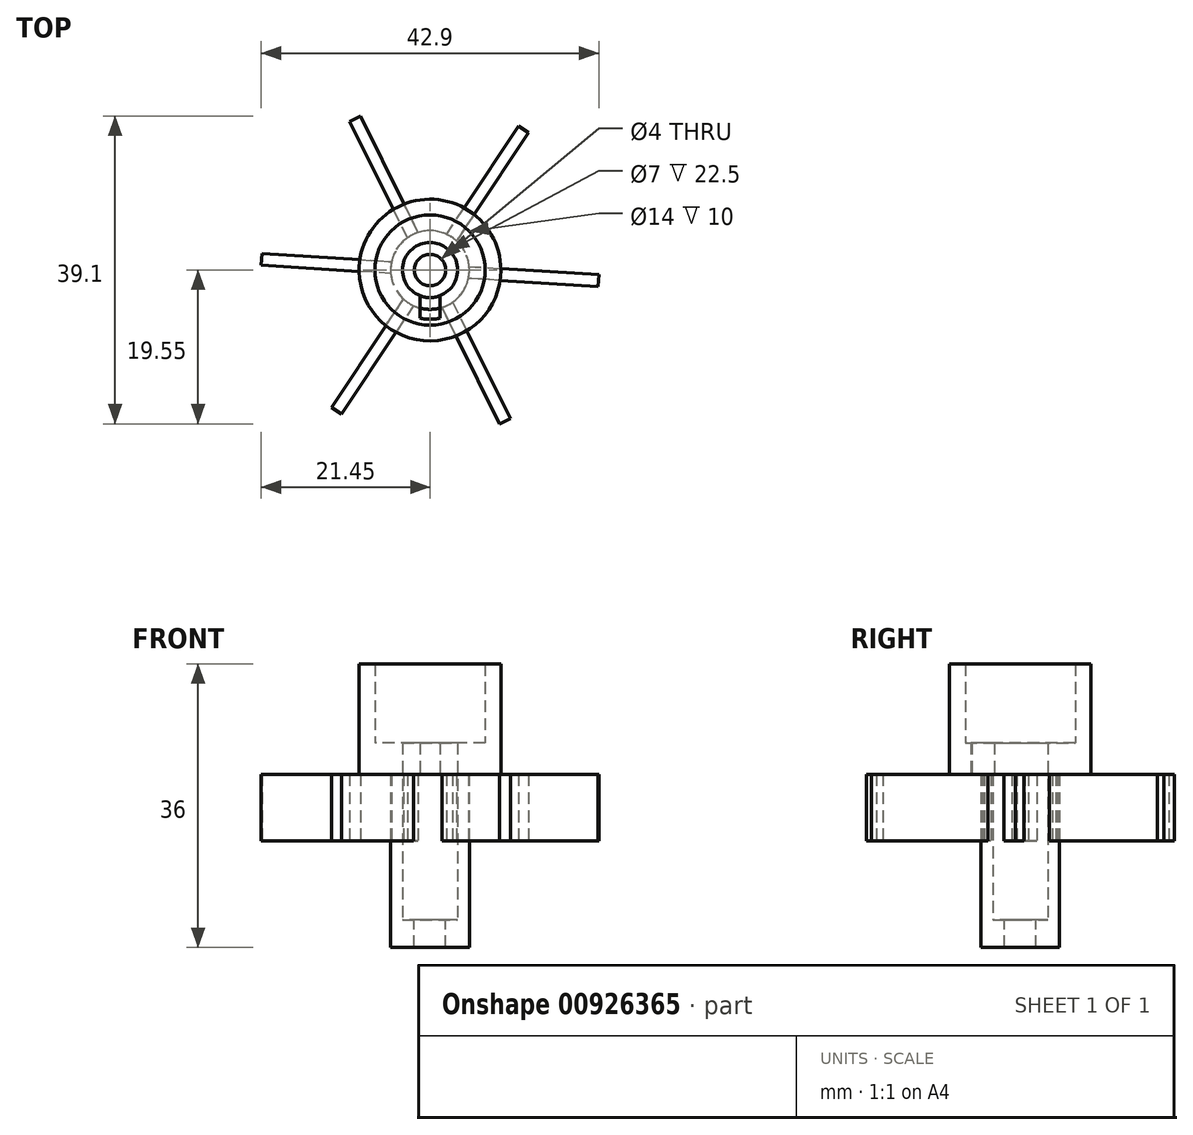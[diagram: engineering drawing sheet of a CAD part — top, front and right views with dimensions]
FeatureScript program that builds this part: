
annotation { "Feature Type Name" : "Feature", "Feature Type Description" : "" }
export const myFeature = defineFeature(function(context is Context, id is Id, definition is map)
    precondition{}
    {
        {
            var Q0;
            Q0=qCreatedBy(makeId("Top.planeOp"),FACE);
            var sketch = newSketch(context, id + "F0", { "sketchPlane" : qUnion([Q0])});
            skCircle(sketch, "E0", {"center": v(0, 0) * mm, "radius": 5 * mm});
            skCircle(sketch, "E1", {"center": v(0, 0) * mm, "radius": 3.5 * mm});
            skLineSegment(sketch, "E2", {"start": v(0, 0) * mm, "end": v(-28.81, 1.83) * mm, "construction": true});
            skLineSegment(sketch, "E3", {"start": v(-4.98, -0.44) * mm, "end": v(-21.45, 0.6) * mm});
            skLineSegment(sketch, "E4", {"start": v(-21.45, 0.6) * mm, "end": v(-21.35, 2.1) * mm});
            skLineSegment(sketch, "E5", {"start": v(-21.35, 2.1) * mm, "end": v(-4.89, 1.06) * mm});
            skLineSegment(sketch, "E6.1.0", {"start": v(-12.5, -17.44) * mm, "end": v(-3.36, -3.7) * mm});
            skLineSegment(sketch, "E6.1.1", {"start": v(-2.11, -4.53) * mm, "end": v(-11.25, -18.27) * mm});
            skLineSegment(sketch, "E6.1.2", {"start": v(-11.25, -18.27) * mm, "end": v(-12.5, -17.44) * mm});
            skLineSegment(sketch, "E6.2.0", {"start": v(8.85, -19.55) * mm, "end": v(1.52, -4.76) * mm});
            skLineSegment(sketch, "E6.2.1", {"start": v(2.87, -4.1) * mm, "end": v(10.2, -18.88) * mm});
            skLineSegment(sketch, "E6.2.2", {"start": v(10.2, -18.88) * mm, "end": v(8.85, -19.55) * mm});
            skLineSegment(sketch, "E6.3.0", {"start": v(21.35, -2.1) * mm, "end": v(4.89, -1.06) * mm});
            skLineSegment(sketch, "E6.3.1", {"start": v(4.98, 0.44) * mm, "end": v(21.45, -0.6) * mm});
            skLineSegment(sketch, "E6.3.2", {"start": v(21.45, -0.6) * mm, "end": v(21.35, -2.1) * mm});
            skLineSegment(sketch, "E6.4.0", {"start": v(12.5, 17.44) * mm, "end": v(3.36, 3.7) * mm});
            skLineSegment(sketch, "E6.4.1", {"start": v(2.11, 4.53) * mm, "end": v(11.25, 18.27) * mm});
            skLineSegment(sketch, "E6.4.2", {"start": v(11.25, 18.27) * mm, "end": v(12.5, 17.44) * mm});
            skLineSegment(sketch, "E6.5.0", {"start": v(-8.85, 19.55) * mm, "end": v(-1.52, 4.76) * mm});
            skLineSegment(sketch, "E6.5.1", {"start": v(-2.87, 4.1) * mm, "end": v(-10.2, 18.88) * mm});
            skLineSegment(sketch, "E6.5.2", {"start": v(-10.2, 18.88) * mm, "end": v(-8.85, 19.55) * mm});
            skCircle(sketch, "E7", {"center": v(0, 0) * mm, "radius": 2 * mm});
            skSolve(sketch);
        }
        {
            var Q0;
            {var subQ0=sQuery(id+"F0.wireOp",EDGE,"E3");Q0=makeQuery(id+"F0.imprint","IMPRINT",FACE,{"disambiguationData":[TD([[makeQuery(id+"F0.imprint","IMPRINT",EDGE,{"derivedFrom":subQ0}),-1.0]])]});}
            var Q1;
            Q1=makeQuery(id+"F0.imprint","IMPRINT",FACE,{"disambiguationData":[TD([[makeQuery(id+"F0.imprint","IMPRINT",EDGE,{"derivedFrom":sQuery(id+"F0.wireOp",EDGE,"E1")}),-1.0]])]});
            var Q2;
            {var subQ0=sQuery(id+"F0.wireOp",EDGE,"E6.5.0");Q2=makeQuery(id+"F0.imprint","IMPRINT",FACE,{"disambiguationData":[TD([[makeQuery(id+"F0.imprint","IMPRINT",EDGE,{"derivedFrom":subQ0}),-1.0]])]});}
            var Q3;
            {var subQ0=sQuery(id+"F0.wireOp",EDGE,"E6.4.0");Q3=makeQuery(id+"F0.imprint","IMPRINT",FACE,{"disambiguationData":[TD([[makeQuery(id+"F0.imprint","IMPRINT",EDGE,{"derivedFrom":subQ0}),-1.0]])]});}
            var Q4;
            {var subQ0=sQuery(id+"F0.wireOp",EDGE,"E6.3.0");Q4=makeQuery(id+"F0.imprint","IMPRINT",FACE,{"disambiguationData":[TD([[makeQuery(id+"F0.imprint","IMPRINT",EDGE,{"derivedFrom":subQ0}),-1.0]])]});}
            var Q5;
            {var subQ0=sQuery(id+"F0.wireOp",EDGE,"E6.2.0");Q5=makeQuery(id+"F0.imprint","IMPRINT",FACE,{"disambiguationData":[TD([[makeQuery(id+"F0.imprint","IMPRINT",EDGE,{"derivedFrom":subQ0}),-1.0]])]});}
            var Q6;
            {var subQ0=sQuery(id+"F0.wireOp",EDGE,"E6.1.0");Q6=makeQuery(id+"F0.imprint","IMPRINT",FACE,{"disambiguationData":[TD([[makeQuery(id+"F0.imprint","IMPRINT",EDGE,{"derivedFrom":subQ0}),-1.0]])]});}
            extrude(context, id + "F1", {"entities" : qUnion([Q0, Q1, Q2, Q3, Q4, Q5, Q6]), "depth" : 8.5 * mm, "offsetDistance" : 25 * mm});
        }
        {
            var Q0;
            Q0=makeQuery(id+"F0.imprint","IMPRINT",FACE,{"disambiguationData":[TD([[makeQuery(id+"F0.imprint","IMPRINT",EDGE,{"derivedFrom":sQuery(id+"F0.wireOp",EDGE,"E1")}),1.0]])]});
            var Q1;
            Q1=makeQuery(id+"F0.imprint","IMPRINT",FACE,{"disambiguationData":[TD([[makeQuery(id+"F0.imprint","IMPRINT",EDGE,{"derivedFrom":sQuery(id+"F0.wireOp",EDGE,"E1")}),-1.0]])]});
            extrude(context, id + "F2", {"entities" : qUnion([Q0, Q1]), "operationType" : NewBodyOperationType.ADD, "oppositeDirection" : true, "depth" : 13.5 * mm, "offsetDistance" : 25 * mm});
        }
        {
            var Q0;
            Q0=makeQuery(id+"F1.opExtrude","CAP_FACE",FACE,{"disambiguationData":[OSD([sQuery(id+"F0.wireOp",EDGE,"E0"),sQuery(id+"F0.wireOp",EDGE,"E1"),sQuery(id+"F0.wireOp",EDGE,"E3"),sQuery(id+"F0.wireOp",EDGE,"E4"),sQuery(id+"F0.wireOp",EDGE,"E5"),sQuery(id+"F0.wireOp",EDGE,"E6.1.0"),sQuery(id+"F0.wireOp",EDGE,"E6.1.1"),sQuery(id+"F0.wireOp",EDGE,"E6.1.2"),sQuery(id+"F0.wireOp",EDGE,"E6.2.0"),sQuery(id+"F0.wireOp",EDGE,"E6.2.1"),sQuery(id+"F0.wireOp",EDGE,"E6.2.2"),sQuery(id+"F0.wireOp",EDGE,"E6.3.0"),sQuery(id+"F0.wireOp",EDGE,"E6.3.1"),sQuery(id+"F0.wireOp",EDGE,"E6.3.2"),sQuery(id+"F0.wireOp",EDGE,"E6.4.0"),sQuery(id+"F0.wireOp",EDGE,"E6.4.1"),sQuery(id+"F0.wireOp",EDGE,"E6.4.2"),sQuery(id+"F0.wireOp",EDGE,"E6.5.0"),sQuery(id+"F0.wireOp",EDGE,"E6.5.1"),sQuery(id+"F0.wireOp",EDGE,"E6.5.2")])],"isStart":false});
            cPlane(context, id + "F3", {"entities" : qUnion([Q0]), "cplaneType" : CPlaneType.OFFSET, "offset" : 0 * mm, "width" : 150 * mm, "height" : 150 * mm});
        }
        {
            var Q0;
            Q0=qCreatedBy(id+"F3.planeOp",FACE);
            var sketch = newSketch(context, id + "F4", { "sketchPlane" : qUnion([Q0])});
            skCircle(sketch, "E8", {"center": v(0, 0) * mm, "radius": 9 * mm});
            skCircle(sketch, "E9", {"center": v(0, 0) * mm, "radius": 3.5 * mm});
            skCircle(sketch, "E10", {"center": v(0, 0) * mm, "radius": 6.25 * mm});
            skCircle(sketch, "E11", {"center": v(0, 0) * mm, "radius": 7 * mm});
            skLineSegment(sketch, "E12.bottom", {"start": v(-1.25, -3.27) * mm, "end": v(1.25, -3.27) * mm});
            skLineSegment(sketch, "E12.top", {"start": v(-1.25, -6.25) * mm, "end": v(1.25, -6.25) * mm});
            skLineSegment(sketch, "E12.left", {"start": v(-1.25, -3.27) * mm, "end": v(-1.25, -6.25) * mm});
            skLineSegment(sketch, "E12.right", {"start": v(1.25, -3.27) * mm, "end": v(1.25, -6.25) * mm});
            skLineSegment(sketch, "E13", {"start": v(0, 0) * mm, "end": v(0, -9.75) * mm, "construction": true});
            skPoint(sketch, "E14", {"position": v(0, -6.25) * mm});
            skSolve(sketch);
        }
        {
            var Q0;
            Q0=makeQuery(id+"F4.imprint","IMPRINT",FACE,{"disambiguationData":[TD([[makeQuery(id+"F4.imprint","IMPRINT",EDGE,{"derivedFrom":sQuery(id+"F4.wireOp",EDGE,"E8")}),1.0]])]});
            var Q1;
            Q1=makeQuery(id+"F4.imprint","IMPRINT",FACE,{"disambiguationData":[TD([[makeQuery(id+"F4.imprint","IMPRINT",EDGE,{"derivedFrom":sQuery(id+"F4.wireOp",EDGE,"E9")}),-1.0]])]});
            var Q2;
            Q2=makeQuery(id+"F4.imprint","IMPRINT",FACE,{"disambiguationData":[TD([[makeQuery(id+"F4.imprint","IMPRINT",EDGE,{"derivedFrom":sQuery(id+"F4.wireOp",EDGE,"E10")}),-1.0]])]});
            var Q3;
            Q3=makeQuery(id+"F4.imprint","IMPRINT",FACE,{"disambiguationData":[TD([[makeQuery(id+"F4.imprint","IMPRINT",EDGE,{"derivedFrom":sQuery(id+"F4.wireOp",EDGE,"E11")}),1.0]])]});
            extrude(context, id + "F5", {"entities" : qUnion([Q0, Q1, Q2, Q3]), "operationType" : NewBodyOperationType.ADD, "depth" : 1 * mm, "offsetDistance" : 25 * mm});
        }
        {
            var Q0;
            Q0=makeQuery(id+"F5.opExtrude","CAP_FACE",FACE,{"disambiguationData":[OSD([sQuery(id+"F4.wireOp",EDGE,"E8"),sQuery(id+"F4.wireOp",EDGE,"E9"),sQuery(id+"F4.wireOp",EDGE,"E10"),sQuery(id+"F4.wireOp",EDGE,"E12.left"),sQuery(id+"F4.wireOp",EDGE,"E12.right")])],"isStart":false});
            extrude(context, id + "F6", {"entities" : qUnion([Q0]), "operationType" : NewBodyOperationType.ADD, "depth" : 3 * mm, "offsetDistance" : 25 * mm});
        }
        {
            var Q0;
            Q0=makeQuery(id+"F4.imprint","IMPRINT",FACE,{"disambiguationData":[TD([[makeQuery(id+"F4.imprint","IMPRINT",EDGE,{"derivedFrom":sQuery(id+"F4.wireOp",EDGE,"E8")}),1.0]])]});
            extrude(context, id + "F7", {"entities" : qUnion([Q0]), "operationType" : NewBodyOperationType.ADD, "depth" : 14 * mm, "offsetDistance" : 25 * mm});
        }
        {
            var Q0;
            Q0=makeQuery(id+"F0.imprint","IMPRINT",FACE,{"disambiguationData":[TD([[makeQuery(id+"F0.imprint","IMPRINT",EDGE,{"derivedFrom":sQuery(id+"F0.wireOp",EDGE,"E1")}),1.0]])]});
            extrude(context, id + "F8", {"entities" : qUnion([Q0]), "operationType" : NewBodyOperationType.REMOVE, "oppositeDirection" : true, "depth" : 10 * mm, "offsetDistance" : 25 * mm});
        }
    });
